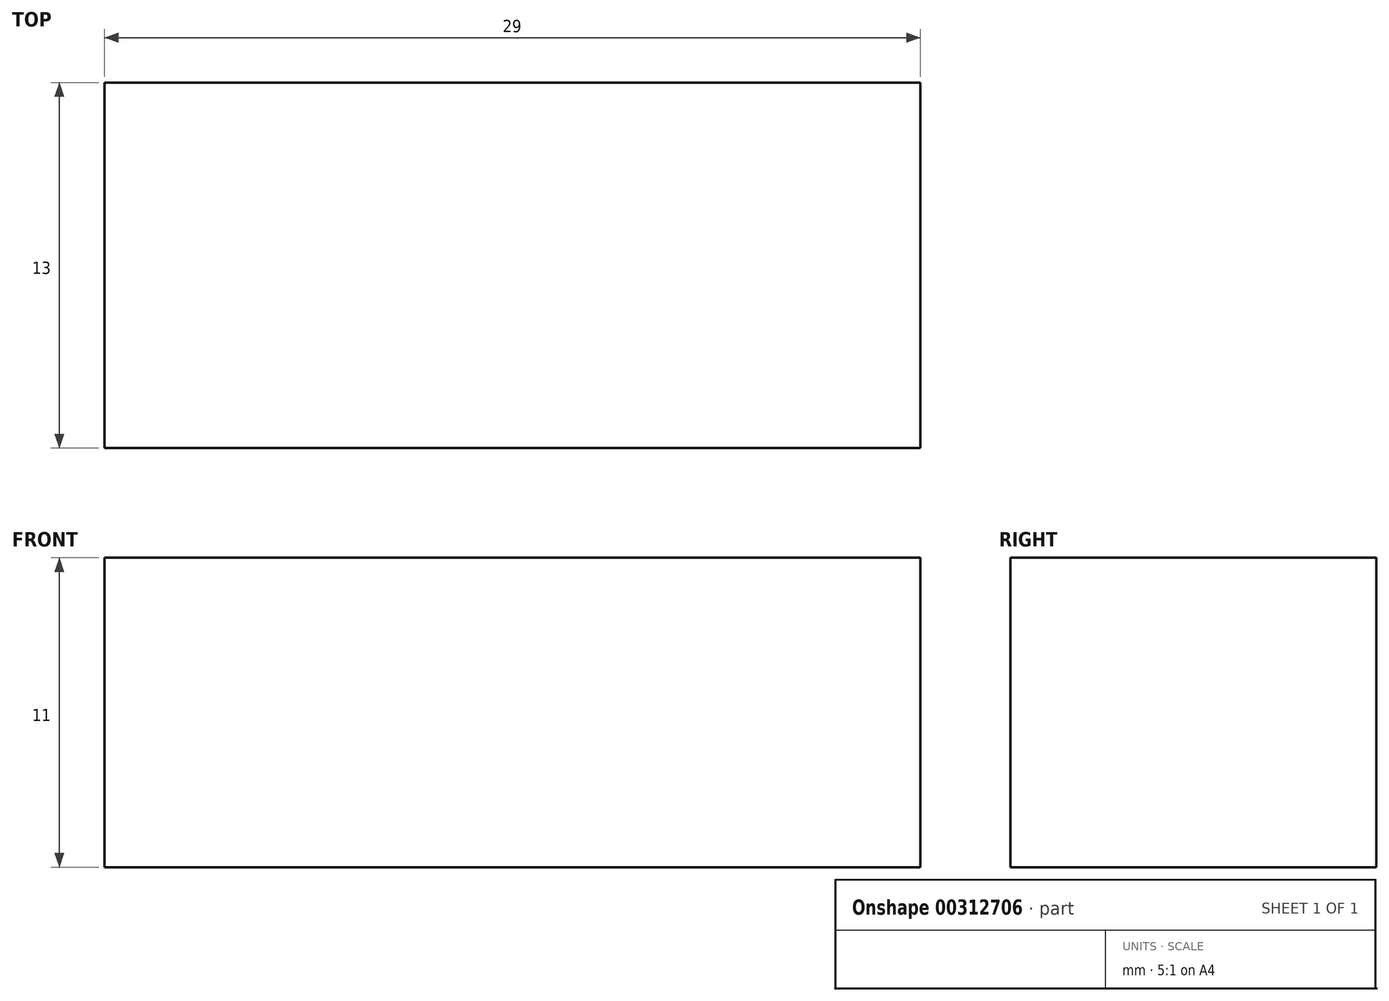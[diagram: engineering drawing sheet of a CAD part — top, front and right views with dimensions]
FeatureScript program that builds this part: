
annotation { "Feature Type Name" : "Feature", "Feature Type Description" : "" }
export const myFeature = defineFeature(function(context is Context, id is Id, definition is map)
    precondition{}
    {
        {
            var Q0;
            Q0=qCreatedBy(makeId("Top.planeOp"),FACE);
            var sketch = newSketch(context, id + "F0", { "sketchPlane" : qUnion([Q0])});
            skLineSegment(sketch, "E0.bottom", {"start": v(0, 0) * mm, "end": v(29, 0) * mm});
            skLineSegment(sketch, "E0.top", {"start": v(0, -13) * mm, "end": v(29, -13) * mm});
            skLineSegment(sketch, "E0.left", {"start": v(0, 0) * mm, "end": v(0, -13) * mm});
            skLineSegment(sketch, "E0.right", {"start": v(29, 0) * mm, "end": v(29, -13) * mm});
            skSolve(sketch);
        }
        {
            var Q0;
            Q0=makeQuery(id+"F0.imprint","IMPRINT",FACE,{"disambiguationData":[TD([[makeQuery(id+"F0.imprint","IMPRINT",EDGE,{"derivedFrom":sQuery(id+"F0.wireOp",EDGE,"E0.bottom")}),-1.0]])]});
            extrude(context, id + "F1", {"entities" : qUnion([Q0]), "depth" : 11 * mm});
        }
    });
